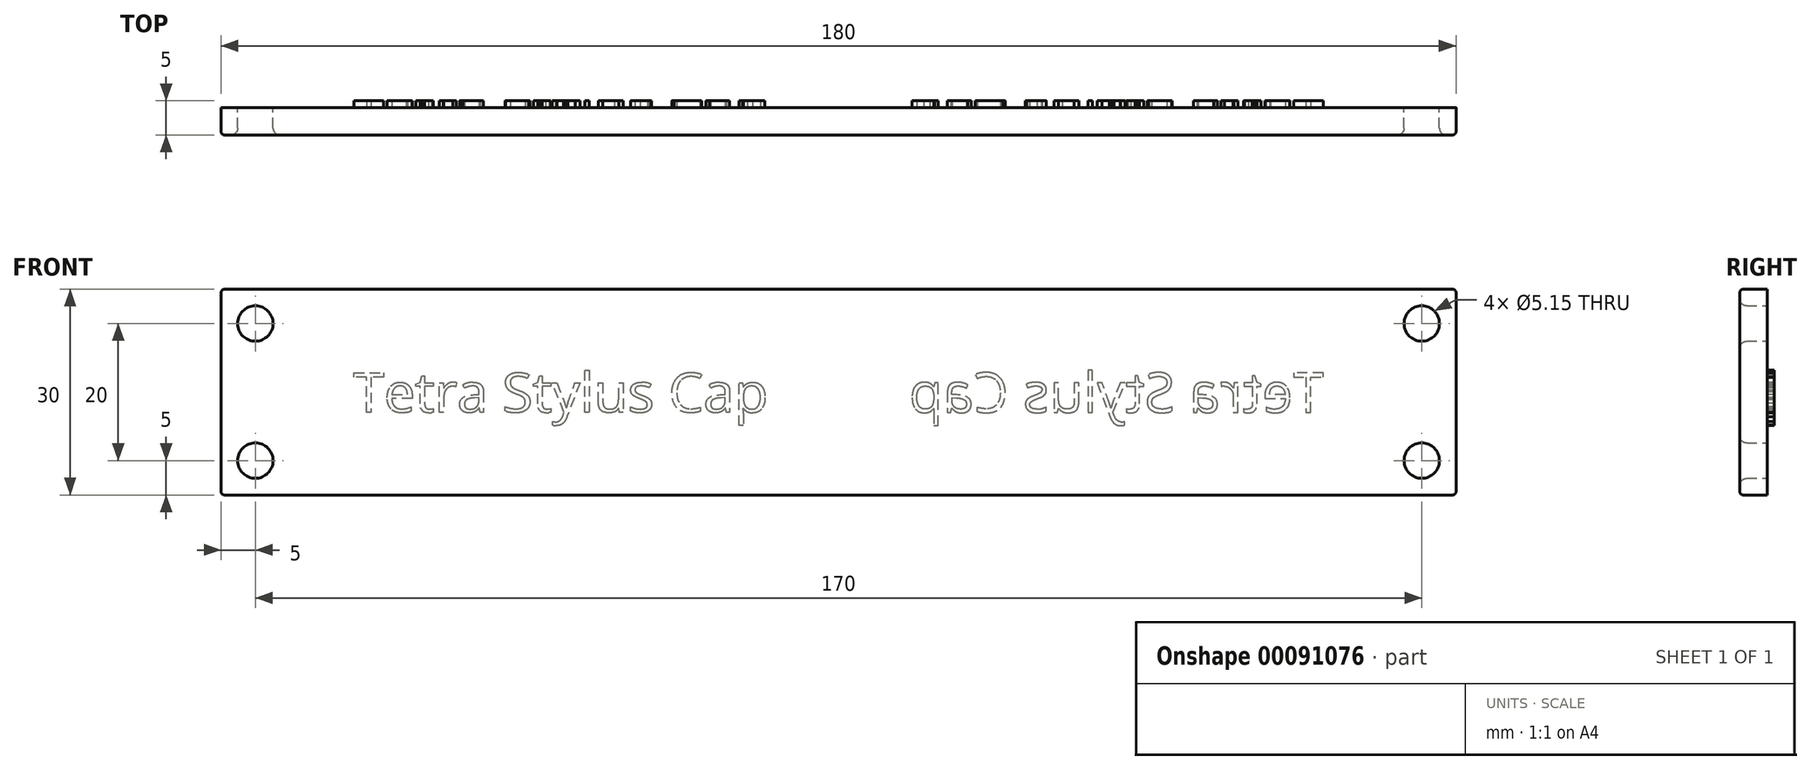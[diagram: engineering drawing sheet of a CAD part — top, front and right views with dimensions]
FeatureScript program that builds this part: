
annotation { "Feature Type Name" : "Feature", "Feature Type Description" : "" }
export const myFeature = defineFeature(function(context is Context, id is Id, definition is map)
    precondition{}
    {
        {
            var Q0;
            Q0=qCreatedBy(makeId("Front.planeOp"),FACE);
            var sketch = newSketch(context, id + "F0", { "sketchPlane" : qUnion([Q0])});
            skLineSegment(sketch, "E0.bottom", {"start": v(-90, -15) * mm, "end": v(90, -15) * mm});
            skLineSegment(sketch, "E0.top", {"start": v(-90, 15) * mm, "end": v(90, 15) * mm});
            skLineSegment(sketch, "E0.left", {"start": v(-90, -15) * mm, "end": v(-90, 15) * mm});
            skLineSegment(sketch, "E0.right", {"start": v(90, -15) * mm, "end": v(90, 15) * mm});
            skPoint(sketch, "E0.middle", {"position": v(0, 0) * mm});
            skCircle(sketch, "E1", {"center": v(-85, 10) * mm, "radius": 2.58 * mm});
            skPoint(sketch, "E2.start.orphan", {"position": v(-90, 0) * mm});
            skPoint(sketch, "E3.orphan", {"position": v(0, 15) * mm});
            skPoint(sketch, "E4.end.orphan", {"position": v(0, -15) * mm});
            skLineSegment(sketch, "E5", {"start": v(-90, 0) * mm, "end": v(0, 0) * mm, "construction": true});
            skLineSegment(sketch, "E6", {"start": v(0, 15) * mm, "end": v(0, -15) * mm, "construction": true});
            skCircle(sketch, "E7.MirrorC", {"center": v(-85, -10) * mm, "radius": 2.58 * mm});
            skCircle(sketch, "E8.MirrorC", {"center": v(85, 10) * mm, "radius": 2.58 * mm});
            skCircle(sketch, "E9.MirrorC", {"center": v(85, -10) * mm, "radius": 2.58 * mm});
            skSolve(sketch);
        }
        {
            var Q0;
            Q0=makeQuery(id+"F0.imprint","IMPRINT",FACE,{"disambiguationData":[TD([[makeQuery(id+"F0.imprint","IMPRINT",EDGE,{"derivedFrom":sQuery(id+"F0.wireOp",EDGE,"E0.bottom")}),1.0]])]});
            extrude(context, id + "F1", {"entities" : qUnion([Q0]), "depth" : 4 * mm});
        }
        {
            var Q0;
            Q0=makeQuery(id+"F1.opExtrude","CAP_EDGE",EDGE,{"disambiguationData":[OSD([sQuery(id+"F0.wireOp",EDGE,"E1")])],"isStart":false});
            var Q1;
            Q1=makeQuery(id+"F1.opExtrude","CAP_EDGE",EDGE,{"disambiguationData":[OSD([sQuery(id+"F0.wireOp",EDGE,"f5b72a5b-8583-449a-bdbf-9ac5a681e1fd0.MirrorC")])],"isStart":false});
            var Q2;
            Q2=makeQuery(id+"F1.opExtrude","CAP_EDGE",EDGE,{"disambiguationData":[OSD([sQuery(id+"F0.wireOp",EDGE,"2623e306-60f4-4522-aa65-1e3e8c2cf5b60.MirrorC")])],"isStart":false});
            var Q3;
            Q3=makeQuery(id+"F1.opExtrude","CAP_EDGE",EDGE,{"disambiguationData":[OSD([sQuery(id+"F0.wireOp",EDGE,"be81a34d-1d50-4ce7-a7a8-4484a1701fac0.MirrorC")])],"isStart":false});
            var Q4;
            Q4=makeQuery(id+"F1.opExtrude","CAP_EDGE",EDGE,{"disambiguationData":[OSD([sQuery(id+"F0.wireOp",EDGE,"E7.MirrorC")])],"isStart":false});
            var Q5;
            Q5=makeQuery(id+"F1.opExtrude","CAP_EDGE",EDGE,{"disambiguationData":[OSD([sQuery(id+"F0.wireOp",EDGE,"E8.MirrorC")])],"isStart":false});
            var Q6;
            Q6=makeQuery(id+"F1.opExtrude","CAP_EDGE",EDGE,{"disambiguationData":[OSD([sQuery(id+"F0.wireOp",EDGE,"E9.MirrorC")])],"isStart":false});
            fillet(context, id + "F2", {"entities" : qUnion([Q0, Q1, Q2, Q3, Q4, Q5, Q6]), "radius" : 1 * mm, "tangentPropagation" : true, "allowEdgeOverflow" : false});
        }
        {
            var Q0;
            Q0=makeQuery(id+"F1.opExtrude","CAP_EDGE",EDGE,{"disambiguationData":[OSD([sQuery(id+"F0.wireOp",EDGE,"E0.top")])],"isStart":false});
            var Q1;
            Q1=makeQuery(id+"F1.opExtrude","CAP_EDGE",EDGE,{"disambiguationData":[OSD([sQuery(id+"F0.wireOp",EDGE,"E0.left")])],"isStart":false});
            var Q2;
            Q2=makeQuery(id+"F1.opExtrude","CAP_EDGE",EDGE,{"disambiguationData":[OSD([sQuery(id+"F0.wireOp",EDGE,"E0.bottom")])],"isStart":false});
            var Q3;
            Q3=makeQuery(id+"F1.opExtrude","CAP_EDGE",EDGE,{"disambiguationData":[OSD([sQuery(id+"F0.wireOp",EDGE,"E0.right")])],"isStart":false});
            var Q4;
            Q4=makeQuery(id+"F1.opExtrude","SWEPT_EDGE",EDGE,{"disambiguationData":[OSD([sQuery(id+"F0.wireOp",EDGE,"E0.top"),sQuery(id+"F0.wireOp",EDGE,"E0.left")])]});
            var Q5;
            Q5=makeQuery(id+"F1.opExtrude","SWEPT_EDGE",EDGE,{"disambiguationData":[OSD([sQuery(id+"F0.wireOp",EDGE,"E0.bottom"),sQuery(id+"F0.wireOp",EDGE,"E0.left")])]});
            var Q6;
            Q6=makeQuery(id+"F1.opExtrude","SWEPT_EDGE",EDGE,{"disambiguationData":[OSD([sQuery(id+"F0.wireOp",EDGE,"E0.top"),sQuery(id+"F0.wireOp",EDGE,"E0.right")])]});
            var Q7;
            Q7=makeQuery(id+"F1.opExtrude","SWEPT_EDGE",EDGE,{"disambiguationData":[OSD([sQuery(id+"F0.wireOp",EDGE,"E0.bottom"),sQuery(id+"F0.wireOp",EDGE,"E0.right")])]});
            fillet(context, id + "F3", {"entities" : qUnion([Q0, Q1, Q2, Q3, Q4, Q5, Q6, Q7]), "radius" : .5 * mm, "tangentPropagation" : true, "allowEdgeOverflow" : false});
        }
        {
            var Q0;
            Q0=makeQuery(id+"F1.opExtrude","CAP_FACE",FACE,{"disambiguationData":[OSD([sQuery(id+"F0.wireOp",EDGE,"E0.bottom"),sQuery(id+"F0.wireOp",EDGE,"E0.top"),sQuery(id+"F0.wireOp",EDGE,"E0.left"),sQuery(id+"F0.wireOp",EDGE,"E0.right"),sQuery(id+"F0.wireOp",EDGE,"E1"),sQuery(id+"F0.wireOp",EDGE,"E7.MirrorC"),sQuery(id+"F0.wireOp",EDGE,"E8.MirrorC"),sQuery(id+"F0.wireOp",EDGE,"E9.MirrorC")])],"isStart":true});
            var sketch = newSketch(context, id + "F4", { "sketchPlane" : qUnion([Q0])});
            skText(sketch, "E10", { "text": "Tetra Stylus Cap", "fontName": "OpenSans-Regular.ttf"});
            skLineSegment(sketch, "E11", {"start": v(0, 15) * mm, "end": v(0, -15) * mm, "construction": true});
            const initialGuessF4  = {"E10": [-0.0707, -0.00295, 1, 0, 0.0058]};
            skSetInitialGuess(sketch, initialGuessF4);
            skSolve(sketch);
        }
        {
            var Q0;
            Q0=qSketchRegion(id+"F4",true);
            extrude(context, id + "F5", {"entities" : qUnion([Q0]), "operationType" : NewBodyOperationType.ADD, "depth" : 1 * mm});
        }
        {
            var Q0;
            Q0=makeQuery(id+"F1.opExtrude","SWEPT_BODY",BODY,{"disambiguationData":[OSD([sQuery(id+"F0.wireOp",EDGE,"E0.bottom"),sQuery(id+"F0.wireOp",EDGE,"E0.top"),sQuery(id+"F0.wireOp",EDGE,"E0.left"),sQuery(id+"F0.wireOp",EDGE,"E0.right"),sQuery(id+"F0.wireOp",EDGE,"E1"),sQuery(id+"F0.wireOp",EDGE,"E7.MirrorC"),sQuery(id+"F0.wireOp",EDGE,"E8.MirrorC"),sQuery(id+"F0.wireOp",EDGE,"E9.MirrorC")])]});
            var Q1;
            Q1=makeQuery(id+"F5.opExtrude","SWEPT_FACE",FACE,{"disambiguationData":[OSD([sQuery(id+"F4.wireOp",EDGE,"E10.sketch_text.stroke-94")])]});
            var Q2;
            Q2=makeQuery(id+"F5.opExtrude","SWEPT_FACE",FACE,{"disambiguationData":[OSD([sQuery(id+"F4.wireOp",EDGE,"E10.sketch_text.stroke-169")])]});
            var Q3;
            Q3=makeQuery(id+"F5.opExtrude","SWEPT_FACE",FACE,{"disambiguationData":[OSD([sQuery(id+"F4.wireOp",EDGE,"E10.sketch_text.stroke-185")])]});
            var Q4;
            Q4=makeQuery(id+"F5.opExtrude","SWEPT_FACE",FACE,{"disambiguationData":[OSD([sQuery(id+"F4.wireOp",EDGE,"E10.sketch_text.stroke-125")])]});
            var Q5;
            Q5=makeQuery(id+"F5.opExtrude","SWEPT_FACE",FACE,{"disambiguationData":[OSD([sQuery(id+"F4.wireOp",EDGE,"E10.sketch_text.stroke-155")])]});
            var Q6;
            Q6=makeQuery(id+"F5.opExtrude","SWEPT_FACE",FACE,{"disambiguationData":[OSD([sQuery(id+"F4.wireOp",EDGE,"E10.sketch_text.stroke-65")])]});
            var Q7;
            Q7=makeQuery(id+"F5.opExtrude","SWEPT_FACE",FACE,{"disambiguationData":[OSD([sQuery(id+"F4.wireOp",EDGE,"E10.sketch_text.stroke-81")])]});
            var Q8;
            Q8=makeQuery(id+"F5.opExtrude","SWEPT_FACE",FACE,{"disambiguationData":[OSD([sQuery(id+"F4.wireOp",EDGE,"E10.sketch_text.stroke-67")])]});
            var Q9;
            Q9=makeQuery(id+"F5.opExtrude","SWEPT_FACE",FACE,{"disambiguationData":[OSD([sQuery(id+"F4.wireOp",EDGE,"E10.sketch_text.stroke-99")])]});
            var Q10;
            Q10=makeQuery(id+"F5.opExtrude","SWEPT_FACE",FACE,{"disambiguationData":[OSD([sQuery(id+"F4.wireOp",EDGE,"E10.sketch_text.stroke-127")])]});
            var Q11;
            Q11=makeQuery(id+"F5.opExtrude","SWEPT_FACE",FACE,{"disambiguationData":[OSD([sQuery(id+"F4.wireOp",EDGE,"E10.sketch_text.stroke-10")])]});
            var Q12;
            Q12=makeQuery(id+"F5.opExtrude","CAP_FACE",FACE,{"disambiguationData":[OSD([sQuery(id+"F4.wireOp",EDGE,"E10.sketch_text.stroke-9"),sQuery(id+"F4.wireOp",EDGE,"E10.sketch_text.stroke-10"),sQuery(id+"F4.wireOp",EDGE,"E10.sketch_text.stroke-11"),sQuery(id+"F4.wireOp",EDGE,"E10.sketch_text.stroke-12")])],"isStart":false});
            var Q13;
            Q13=makeQuery(id+"F5.opExtrude","SWEPT_FACE",FACE,{"disambiguationData":[OSD([sQuery(id+"F4.wireOp",EDGE,"E10.sketch_text.stroke-154")])]});
            var Q14;
            Q14=makeQuery(id+"F5.opExtrude","SWEPT_FACE",FACE,{"disambiguationData":[OSD([sQuery(id+"F4.wireOp",EDGE,"E10.sketch_text.stroke-1")])]});
            var Q15;
            Q15=makeQuery(id+"F5.opExtrude","CAP_FACE",FACE,{"disambiguationData":[OSD([sQuery(id+"F4.wireOp",EDGE,"E10.sketch_text.stroke-124"),sQuery(id+"F4.wireOp",EDGE,"E10.sketch_text.stroke-125"),sQuery(id+"F4.wireOp",EDGE,"E10.sketch_text.stroke-126"),sQuery(id+"F4.wireOp",EDGE,"E10.sketch_text.stroke-127"),sQuery(id+"F4.wireOp",EDGE,"E10.sketch_text.stroke-128"),sQuery(id+"F4.wireOp",EDGE,"E10.sketch_text.stroke-129"),sQuery(id+"F4.wireOp",EDGE,"E10.sketch_text.stroke-130"),sQuery(id+"F4.wireOp",EDGE,"E10.sketch_text.stroke-131"),sQuery(id+"F4.wireOp",EDGE,"E10.sketch_text.stroke-132"),sQuery(id+"F4.wireOp",EDGE,"E10.sketch_text.stroke-133"),sQuery(id+"F4.wireOp",EDGE,"E10.sketch_text.stroke-134"),sQuery(id+"F4.wireOp",EDGE,"E10.sketch_text.stroke-135"),sQuery(id+"F4.wireOp",EDGE,"E10.sketch_text.stroke-136"),sQuery(id+"F4.wireOp",EDGE,"E10.sketch_text.stroke-137"),sQuery(id+"F4.wireOp",EDGE,"E10.sketch_text.stroke-138")])],"isStart":false});
            var Q16;
            Q16=makeQuery(id+"F5.opExtrude","CAP_FACE",FACE,{"disambiguationData":[OSD([sQuery(id+"F4.wireOp",EDGE,"E10.sketch_text.stroke-34"),sQuery(id+"F4.wireOp",EDGE,"E10.sketch_text.stroke-35"),sQuery(id+"F4.wireOp",EDGE,"E10.sketch_text.stroke-36"),sQuery(id+"F4.wireOp",EDGE,"E10.sketch_text.stroke-37"),sQuery(id+"F4.wireOp",EDGE,"E10.sketch_text.stroke-38"),sQuery(id+"F4.wireOp",EDGE,"E10.sketch_text.stroke-39"),sQuery(id+"F4.wireOp",EDGE,"E10.sketch_text.stroke-40"),sQuery(id+"F4.wireOp",EDGE,"E10.sketch_text.stroke-41"),sQuery(id+"F4.wireOp",EDGE,"E10.sketch_text.stroke-42"),sQuery(id+"F4.wireOp",EDGE,"E10.sketch_text.stroke-43"),sQuery(id+"F4.wireOp",EDGE,"E10.sketch_text.stroke-44"),sQuery(id+"F4.wireOp",EDGE,"E10.sketch_text.stroke-45"),sQuery(id+"F4.wireOp",EDGE,"E10.sketch_text.stroke-46"),sQuery(id+"F4.wireOp",EDGE,"E10.sketch_text.stroke-47"),sQuery(id+"F4.wireOp",EDGE,"E10.sketch_text.stroke-48"),sQuery(id+"F4.wireOp",EDGE,"E10.sketch_text.stroke-49"),sQuery(id+"F4.wireOp",EDGE,"E10.sketch_text.stroke-50"),sQuery(id+"F4.wireOp",EDGE,"E10.sketch_text.stroke-51"),sQuery(id+"F4.wireOp",EDGE,"E10.sketch_text.stroke-52"),sQuery(id+"F4.wireOp",EDGE,"E10.sketch_text.stroke-53"),sQuery(id+"F4.wireOp",EDGE,"E10.sketch_text.stroke-54"),sQuery(id+"F4.wireOp",EDGE,"E10.sketch_text.stroke-55"),sQuery(id+"F4.wireOp",EDGE,"E10.sketch_text.stroke-56"),sQuery(id+"F4.wireOp",EDGE,"E10.sketch_text.stroke-57"),sQuery(id+"F4.wireOp",EDGE,"E10.sketch_text.stroke-58"),sQuery(id+"F4.wireOp",EDGE,"E10.sketch_text.stroke-59"),sQuery(id+"F4.wireOp",EDGE,"E10.sketch_text.stroke-60")])],"isStart":false});
            var Q17;
            Q17=makeQuery(id+"F5.opExtrude","SWEPT_FACE",FACE,{"disambiguationData":[OSD([sQuery(id+"F4.wireOp",EDGE,"E10.sketch_text.stroke-50")])]});
            var Q18;
            Q18=makeQuery(id+"F5.opExtrude","SWEPT_FACE",FACE,{"disambiguationData":[OSD([sQuery(id+"F4.wireOp",EDGE,"E10.sketch_text.stroke-2")])]});
            var Q19;
            Q19=makeQuery(id+"F5.opExtrude","SWEPT_FACE",FACE,{"disambiguationData":[OSD([sQuery(id+"F4.wireOp",EDGE,"E10.sketch_text.stroke-3")])]});
            var Q20;
            Q20=makeQuery(id+"F5.opExtrude","SWEPT_FACE",FACE,{"disambiguationData":[OSD([sQuery(id+"F4.wireOp",EDGE,"E10.sketch_text.stroke-5")])]});
            var Q21;
            Q21=makeQuery(id+"F5.opExtrude","SWEPT_FACE",FACE,{"disambiguationData":[OSD([sQuery(id+"F4.wireOp",EDGE,"E10.sketch_text.stroke-8")])]});
            var Q22;
            Q22=makeQuery(id+"F5.opExtrude","SWEPT_FACE",FACE,{"disambiguationData":[OSD([sQuery(id+"F4.wireOp",EDGE,"E10.sketch_text.stroke-98")])]});
            var Q23;
            Q23=makeQuery(id+"F5.opExtrude","SWEPT_FACE",FACE,{"disambiguationData":[OSD([sQuery(id+"F4.wireOp",EDGE,"E10.sketch_text.stroke-66")])]});
            var Q24;
            Q24=makeQuery(id+"F5.opExtrude","SWEPT_FACE",FACE,{"disambiguationData":[OSD([sQuery(id+"F4.wireOp",EDGE,"E10.sketch_text.stroke-153")])]});
            var Q25;
            Q25=makeQuery(id+"F5.opExtrude","SWEPT_FACE",FACE,{"disambiguationData":[OSD([sQuery(id+"F4.wireOp",EDGE,"E10.sketch_text.stroke-126")])]});
            var Q26;
            Q26=makeQuery(id+"F5.opExtrude","SWEPT_FACE",FACE,{"disambiguationData":[OSD([sQuery(id+"F4.wireOp",EDGE,"E10.sketch_text.stroke-183")])]});
            var Q27;
            Q27=makeQuery(id+"F5.opExtrude","SWEPT_FACE",FACE,{"disambiguationData":[OSD([sQuery(id+"F4.wireOp",EDGE,"E10.sketch_text.stroke-109")])]});
            var Q28;
            Q28=makeQuery(id+"F5.opExtrude","SWEPT_FACE",FACE,{"disambiguationData":[OSD([sQuery(id+"F4.wireOp",EDGE,"E10.sketch_text.stroke-186")])]});
            var Q29;
            Q29=makeQuery(id+"F5.opExtrude","SWEPT_FACE",FACE,{"disambiguationData":[OSD([sQuery(id+"F4.wireOp",EDGE,"E10.sketch_text.stroke-79")])]});
            var Q30;
            Q30=makeQuery(id+"F5.opExtrude","SWEPT_FACE",FACE,{"disambiguationData":[OSD([sQuery(id+"F4.wireOp",EDGE,"E10.sketch_text.stroke-110")])]});
            var Q31;
            Q31=makeQuery(id+"F5.opExtrude","SWEPT_FACE",FACE,{"disambiguationData":[OSD([sQuery(id+"F4.wireOp",EDGE,"E10.sketch_text.stroke-38")])]});
            var Q32;
            Q32=makeQuery(id+"F5.opExtrude","SWEPT_FACE",FACE,{"disambiguationData":[OSD([sQuery(id+"F4.wireOp",EDGE,"E10.sketch_text.stroke-24")])]});
            var Q33;
            Q33=makeQuery(id+"F5.opExtrude","SWEPT_FACE",FACE,{"disambiguationData":[OSD([sQuery(id+"F4.wireOp",EDGE,"E10.sketch_text.stroke-12")])]});
            var Q34;
            Q34=makeQuery(id+"F5.opExtrude","SWEPT_FACE",FACE,{"disambiguationData":[OSD([sQuery(id+"F4.wireOp",EDGE,"E10.sketch_text.stroke-100")])]});
            var Q35;
            Q35=makeQuery(id+"F5.opExtrude","SWEPT_FACE",FACE,{"disambiguationData":[OSD([sQuery(id+"F4.wireOp",EDGE,"E10.sketch_text.stroke-158")])]});
            var Q36;
            Q36=makeQuery(id+"F5.opExtrude","SWEPT_FACE",FACE,{"disambiguationData":[OSD([sQuery(id+"F4.wireOp",EDGE,"E10.sketch_text.stroke-142")])]});
            var Q37;
            Q37=makeQuery(id+"F5.opExtrude","SWEPT_FACE",FACE,{"disambiguationData":[OSD([sQuery(id+"F4.wireOp",EDGE,"E10.sketch_text.stroke-54")])]});
            var Q38;
            Q38=makeQuery(id+"F5.opExtrude","SWEPT_FACE",FACE,{"disambiguationData":[OSD([sQuery(id+"F4.wireOp",EDGE,"E10.sketch_text.stroke-25")])]});
            var Q39;
            Q39=makeQuery(id+"F5.opExtrude","SWEPT_FACE",FACE,{"disambiguationData":[OSD([sQuery(id+"F4.wireOp",EDGE,"E10.sketch_text.stroke-101")])]});
            var Q40;
            Q40=makeQuery(id+"F5.opExtrude","SWEPT_FACE",FACE,{"disambiguationData":[OSD([sQuery(id+"F4.wireOp",EDGE,"E10.sketch_text.stroke-69")])]});
            var Q41;
            Q41=makeQuery(id+"F5.opExtrude","SWEPT_FACE",FACE,{"disambiguationData":[OSD([sQuery(id+"F4.wireOp",EDGE,"E10.sketch_text.stroke-159")])]});
            var Q42;
            Q42=makeQuery(id+"F5.opExtrude","SWEPT_FACE",FACE,{"disambiguationData":[OSD([sQuery(id+"F4.wireOp",EDGE,"E10.sketch_text.stroke-85")])]});
            var Q43;
            Q43=makeQuery(id+"F5.opExtrude","SWEPT_FACE",FACE,{"disambiguationData":[OSD([sQuery(id+"F4.wireOp",EDGE,"E10.sketch_text.stroke-173")])]});
            var Q44;
            Q44=makeQuery(id+"F5.opExtrude","SWEPT_FACE",FACE,{"disambiguationData":[OSD([sQuery(id+"F4.wireOp",EDGE,"E10.sketch_text.stroke-40")])]});
            var Q45;
            Q45=makeQuery(id+"F5.opExtrude","SWEPT_FACE",FACE,{"disambiguationData":[OSD([sQuery(id+"F4.wireOp",EDGE,"E10.sketch_text.stroke-102")])]});
            var Q46;
            Q46=makeQuery(id+"F5.opExtrude","SWEPT_FACE",FACE,{"disambiguationData":[OSD([sQuery(id+"F4.wireOp",EDGE,"E10.sketch_text.stroke-86")])]});
            var Q47;
            Q47=makeQuery(id+"F5.opExtrude","SWEPT_FACE",FACE,{"disambiguationData":[OSD([sQuery(id+"F4.wireOp",EDGE,"E10.sketch_text.stroke-130")])]});
            var Q48;
            Q48=makeQuery(id+"F5.opExtrude","SWEPT_FACE",FACE,{"disambiguationData":[OSD([sQuery(id+"F4.wireOp",EDGE,"E10.sketch_text.stroke-103")])]});
            var Q49;
            Q49=makeQuery(id+"F5.opExtrude","SWEPT_FACE",FACE,{"disambiguationData":[OSD([sQuery(id+"F4.wireOp",EDGE,"E10.sketch_text.stroke-87")])]});
            var Q50;
            Q50=makeQuery(id+"F5.opExtrude","SWEPT_FACE",FACE,{"disambiguationData":[OSD([sQuery(id+"F4.wireOp",EDGE,"E10.sketch_text.stroke-145")])]});
            var Q51;
            Q51=makeQuery(id+"F5.opExtrude","SWEPT_FACE",FACE,{"disambiguationData":[OSD([sQuery(id+"F4.wireOp",EDGE,"E10.sketch_text.stroke-131")])]});
            var Q52;
            Q52=makeQuery(id+"F5.opExtrude","SWEPT_FACE",FACE,{"disambiguationData":[OSD([sQuery(id+"F4.wireOp",EDGE,"E10.sketch_text.stroke-28")])]});
            var Q53;
            Q53=makeQuery(id+"F5.opExtrude","SWEPT_FACE",FACE,{"disambiguationData":[OSD([sQuery(id+"F4.wireOp",EDGE,"E10.sketch_text.stroke-14")])]});
            var Q54;
            Q54=makeQuery(id+"F5.opExtrude","SWEPT_FACE",FACE,{"disambiguationData":[OSD([sQuery(id+"F4.wireOp",EDGE,"E10.sketch_text.stroke-88")])]});
            var Q55;
            Q55=makeQuery(id+"F5.opExtrude","SWEPT_FACE",FACE,{"disambiguationData":[OSD([sQuery(id+"F4.wireOp",EDGE,"E10.sketch_text.stroke-162")])]});
            var Q56;
            Q56=makeQuery(id+"F5.opExtrude","SWEPT_FACE",FACE,{"disambiguationData":[OSD([sQuery(id+"F4.wireOp",EDGE,"E10.sketch_text.stroke-176")])]});
            var Q57;
            Q57=makeQuery(id+"F5.opExtrude","SWEPT_FACE",FACE,{"disambiguationData":[OSD([sQuery(id+"F4.wireOp",EDGE,"E10.sketch_text.stroke-73")])]});
            var Q58;
            Q58=makeQuery(id+"F5.opExtrude","SWEPT_FACE",FACE,{"disambiguationData":[OSD([sQuery(id+"F4.wireOp",EDGE,"E10.sketch_text.stroke-59")])]});
            var Q59;
            Q59=makeQuery(id+"F5.opExtrude","SWEPT_FACE",FACE,{"disambiguationData":[OSD([sQuery(id+"F4.wireOp",EDGE,"E10.sketch_text.stroke-133")])]});
            var Q60;
            Q60=makeQuery(id+"F5.opExtrude","SWEPT_FACE",FACE,{"disambiguationData":[OSD([sQuery(id+"F4.wireOp",EDGE,"E10.sketch_text.stroke-119")])]});
            var Q61;
            Q61=makeQuery(id+"F5.opExtrude","SWEPT_FACE",FACE,{"disambiguationData":[OSD([sQuery(id+"F4.wireOp",EDGE,"E10.sketch_text.stroke-74")])]});
            var Q62;
            Q62=makeQuery(id+"F5.opExtrude","SWEPT_FACE",FACE,{"disambiguationData":[OSD([sQuery(id+"F4.wireOp",EDGE,"E10.sketch_text.stroke-44")])]});
            var Q63;
            Q63=makeQuery(id+"F5.opExtrude","SWEPT_FACE",FACE,{"disambiguationData":[OSD([sQuery(id+"F4.wireOp",EDGE,"E10.sketch_text.stroke-120")])]});
            var Q64;
            Q64=makeQuery(id+"F5.opExtrude","SWEPT_FACE",FACE,{"disambiguationData":[OSD([sQuery(id+"F4.wireOp",EDGE,"E10.sketch_text.stroke-90")])]});
            var Q65;
            Q65=makeQuery(id+"F5.opExtrude","SWEPT_FACE",FACE,{"disambiguationData":[OSD([sQuery(id+"F4.wireOp",EDGE,"E10.sketch_text.stroke-178")])]});
            var Q66;
            Q66=makeQuery(id+"F5.opExtrude","SWEPT_FACE",FACE,{"disambiguationData":[OSD([sQuery(id+"F4.wireOp",EDGE,"E10.sketch_text.stroke-45")])]});
            var Q67;
            Q67=makeQuery(id+"F5.opExtrude","SWEPT_FACE",FACE,{"disambiguationData":[OSD([sQuery(id+"F4.wireOp",EDGE,"E10.sketch_text.stroke-31")])]});
            var Q68;
            Q68=makeQuery(id+"F5.opExtrude","SWEPT_FACE",FACE,{"disambiguationData":[OSD([sQuery(id+"F4.wireOp",EDGE,"E10.sketch_text.stroke-135")])]});
            var Q69;
            Q69=makeQuery(id+"F5.opExtrude","SWEPT_FACE",FACE,{"disambiguationData":[OSD([sQuery(id+"F4.wireOp",EDGE,"E10.sketch_text.stroke-179")])]});
            var Q70;
            Q70=makeQuery(id+"F5.opExtrude","SWEPT_FACE",FACE,{"disambiguationData":[OSD([sQuery(id+"F4.wireOp",EDGE,"E10.sketch_text.stroke-165")])]});
            var Q71;
            Q71=makeQuery(id+"F5.opExtrude","SWEPT_FACE",FACE,{"disambiguationData":[OSD([sQuery(id+"F4.wireOp",EDGE,"E10.sketch_text.stroke-149")])]});
            var Q72;
            Q72=makeQuery(id+"F5.opExtrude","SWEPT_FACE",FACE,{"disambiguationData":[OSD([sQuery(id+"F4.wireOp",EDGE,"E10.sketch_text.stroke-136")])]});
            var Q73;
            Q73=makeQuery(id+"F5.opExtrude","SWEPT_FACE",FACE,{"disambiguationData":[OSD([sQuery(id+"F4.wireOp",EDGE,"E10.sketch_text.stroke-122")])]});
            var Q74;
            Q74=makeQuery(id+"F5.opExtrude","SWEPT_FACE",FACE,{"disambiguationData":[OSD([sQuery(id+"F4.wireOp",EDGE,"E10.sketch_text.stroke-106")])]});
            var Q75;
            Q75=makeQuery(id+"F5.opExtrude","SWEPT_FACE",FACE,{"disambiguationData":[OSD([sQuery(id+"F4.wireOp",EDGE,"E10.sketch_text.stroke-180")])]});
            var Q76;
            Q76=makeQuery(id+"F5.opExtrude","SWEPT_FACE",FACE,{"disambiguationData":[OSD([sQuery(id+"F4.wireOp",EDGE,"E10.sketch_text.stroke-166")])]});
            var Q77;
            Q77=makeQuery(id+"F5.opExtrude","SWEPT_FACE",FACE,{"disambiguationData":[OSD([sQuery(id+"F4.wireOp",EDGE,"E10.sketch_text.stroke-150")])]});
            var Q78;
            Q78=makeQuery(id+"F5.opExtrude","SWEPT_FACE",FACE,{"disambiguationData":[OSD([sQuery(id+"F4.wireOp",EDGE,"E10.sketch_text.stroke-76")])]});
            var Q79;
            Q79=makeQuery(id+"F5.opExtrude","SWEPT_FACE",FACE,{"disambiguationData":[OSD([sQuery(id+"F4.wireOp",EDGE,"E10.sketch_text.stroke-32")])]});
            var Q80;
            Q80=makeQuery(id+"F5.opExtrude","SWEPT_FACE",FACE,{"disambiguationData":[OSD([sQuery(id+"F4.wireOp",EDGE,"E10.sketch_text.stroke-181")])]});
            var Q81;
            Q81=makeQuery(id+"F5.opExtrude","SWEPT_FACE",FACE,{"disambiguationData":[OSD([sQuery(id+"F4.wireOp",EDGE,"E10.sketch_text.stroke-47")])]});
            var Q82;
            Q82=makeQuery(id+"F5.opExtrude","SWEPT_FACE",FACE,{"disambiguationData":[OSD([sQuery(id+"F4.wireOp",EDGE,"E10.sketch_text.stroke-123")])]});
            var Q83;
            Q83=makeQuery(id+"F5.opExtrude","SWEPT_FACE",FACE,{"disambiguationData":[OSD([sQuery(id+"F4.wireOp",EDGE,"E10.sketch_text.stroke-107")])]});
            var Q84;
            Q84=makeQuery(id+"F5.opExtrude","SWEPT_FACE",FACE,{"disambiguationData":[OSD([sQuery(id+"F4.wireOp",EDGE,"E10.sketch_text.stroke-48")])]});
            var Q85;
            Q85=makeQuery(id+"F5.opExtrude","SWEPT_FACE",FACE,{"disambiguationData":[OSD([sQuery(id+"F4.wireOp",EDGE,"E10.sketch_text.stroke-124")])]});
            var Q86;
            Q86=makeQuery(id+"F5.opExtrude","SWEPT_FACE",FACE,{"disambiguationData":[OSD([sQuery(id+"F4.wireOp",EDGE,"E10.sketch_text.stroke-108")])]});
            var Q87;
            Q87=makeQuery(id+"F5.opExtrude","CAP_FACE",FACE,{"disambiguationData":[OSD([sQuery(id+"F4.wireOp",EDGE,"E10.sketch_text.stroke-139"),sQuery(id+"F4.wireOp",EDGE,"E10.sketch_text.stroke-140"),sQuery(id+"F4.wireOp",EDGE,"E10.sketch_text.stroke-141"),sQuery(id+"F4.wireOp",EDGE,"E10.sketch_text.stroke-142"),sQuery(id+"F4.wireOp",EDGE,"E10.sketch_text.stroke-143"),sQuery(id+"F4.wireOp",EDGE,"E10.sketch_text.stroke-144"),sQuery(id+"F4.wireOp",EDGE,"E10.sketch_text.stroke-145"),sQuery(id+"F4.wireOp",EDGE,"E10.sketch_text.stroke-146"),sQuery(id+"F4.wireOp",EDGE,"E10.sketch_text.stroke-147"),sQuery(id+"F4.wireOp",EDGE,"E10.sketch_text.stroke-148"),sQuery(id+"F4.wireOp",EDGE,"E10.sketch_text.stroke-149"),sQuery(id+"F4.wireOp",EDGE,"E10.sketch_text.stroke-150"),sQuery(id+"F4.wireOp",EDGE,"E10.sketch_text.stroke-151"),sQuery(id+"F4.wireOp",EDGE,"E10.sketch_text.stroke-152"),sQuery(id+"F4.wireOp",EDGE,"E10.sketch_text.stroke-153"),sQuery(id+"F4.wireOp",EDGE,"E10.sketch_text.stroke-154"),sQuery(id+"F4.wireOp",EDGE,"E10.sketch_text.stroke-155"),sQuery(id+"F4.wireOp",EDGE,"E10.sketch_text.stroke-156"),sQuery(id+"F4.wireOp",EDGE,"E10.sketch_text.stroke-157"),sQuery(id+"F4.wireOp",EDGE,"E10.sketch_text.stroke-158"),sQuery(id+"F4.wireOp",EDGE,"E10.sketch_text.stroke-159"),sQuery(id+"F4.wireOp",EDGE,"E10.sketch_text.stroke-160"),sQuery(id+"F4.wireOp",EDGE,"E10.sketch_text.stroke-161"),sQuery(id+"F4.wireOp",EDGE,"E10.sketch_text.stroke-162"),sQuery(id+"F4.wireOp",EDGE,"E10.sketch_text.stroke-163"),sQuery(id+"F4.wireOp",EDGE,"E10.sketch_text.stroke-164"),sQuery(id+"F4.wireOp",EDGE,"E10.sketch_text.stroke-165")])],"isStart":false});
            var Q88;
            Q88=makeQuery(id+"F5.opExtrude","CAP_FACE",FACE,{"disambiguationData":[OSD([sQuery(id+"F4.wireOp",EDGE,"E10.sketch_text.stroke-21"),sQuery(id+"F4.wireOp",EDGE,"E10.sketch_text.stroke-22"),sQuery(id+"F4.wireOp",EDGE,"E10.sketch_text.stroke-23"),sQuery(id+"F4.wireOp",EDGE,"E10.sketch_text.stroke-24"),sQuery(id+"F4.wireOp",EDGE,"E10.sketch_text.stroke-25"),sQuery(id+"F4.wireOp",EDGE,"E10.sketch_text.stroke-26"),sQuery(id+"F4.wireOp",EDGE,"E10.sketch_text.stroke-27"),sQuery(id+"F4.wireOp",EDGE,"E10.sketch_text.stroke-28"),sQuery(id+"F4.wireOp",EDGE,"E10.sketch_text.stroke-29"),sQuery(id+"F4.wireOp",EDGE,"E10.sketch_text.stroke-30"),sQuery(id+"F4.wireOp",EDGE,"E10.sketch_text.stroke-31"),sQuery(id+"F4.wireOp",EDGE,"E10.sketch_text.stroke-32"),sQuery(id+"F4.wireOp",EDGE,"E10.sketch_text.stroke-33")])],"isStart":false});
            var Q89;
            Q89=makeQuery(id+"F5.opExtrude","SWEPT_FACE",FACE,{"disambiguationData":[OSD([sQuery(id+"F4.wireOp",EDGE,"E10.sketch_text.stroke-113")])]});
            var Q90;
            Q90=makeQuery(id+"F5.opExtrude","SWEPT_FACE",FACE,{"disambiguationData":[OSD([sQuery(id+"F4.wireOp",EDGE,"E10.sketch_text.stroke-37")])]});
            var Q91;
            Q91=makeQuery(id+"F5.opExtrude","SWEPT_FACE",FACE,{"disambiguationData":[OSD([sQuery(id+"F4.wireOp",EDGE,"E10.sketch_text.stroke-187")])]});
            var Q92;
            Q92=makeQuery(id+"F5.opExtrude","SWEPT_FACE",FACE,{"disambiguationData":[OSD([sQuery(id+"F4.wireOp",EDGE,"E10.sketch_text.stroke-0")])]});
            var Q93;
            Q93=makeQuery(id+"F5.opExtrude","SWEPT_FACE",FACE,{"disambiguationData":[OSD([sQuery(id+"F4.wireOp",EDGE,"E10.sketch_text.stroke-4")])]});
            var Q94;
            Q94=makeQuery(id+"F5.opExtrude","SWEPT_FACE",FACE,{"disambiguationData":[OSD([sQuery(id+"F4.wireOp",EDGE,"E10.sketch_text.stroke-82")])]});
            var Q95;
            Q95=makeQuery(id+"F5.opExtrude","SWEPT_FACE",FACE,{"disambiguationData":[OSD([sQuery(id+"F4.wireOp",EDGE,"E10.sketch_text.stroke-52")])]});
            var Q96;
            Q96=makeQuery(id+"F5.opExtrude","SWEPT_FACE",FACE,{"disambiguationData":[OSD([sQuery(id+"F4.wireOp",EDGE,"E10.sketch_text.stroke-49")])]});
            var Q97;
            Q97=makeQuery(id+"F5.opExtrude","SWEPT_FACE",FACE,{"disambiguationData":[OSD([sQuery(id+"F4.wireOp",EDGE,"E10.sketch_text.stroke-63")])]});
            var Q98;
            Q98=makeQuery(id+"F5.opExtrude","SWEPT_FACE",FACE,{"disambiguationData":[OSD([sQuery(id+"F4.wireOp",EDGE,"E10.sketch_text.stroke-21")])]});
            var Q99;
            Q99=makeQuery(id+"F5.opExtrude","SWEPT_FACE",FACE,{"disambiguationData":[OSD([sQuery(id+"F4.wireOp",EDGE,"E10.sketch_text.stroke-128")])]});
            var Q100;
            Q100=makeQuery(id+"F5.opExtrude","SWEPT_FACE",FACE,{"disambiguationData":[OSD([sQuery(id+"F4.wireOp",EDGE,"E10.sketch_text.stroke-55")])]});
            var Q101;
            Q101=makeQuery(id+"F5.opExtrude","SWEPT_FACE",FACE,{"disambiguationData":[OSD([sQuery(id+"F4.wireOp",EDGE,"E10.sketch_text.stroke-26")])]});
            var Q102;
            Q102=makeQuery(id+"F5.opExtrude","SWEPT_FACE",FACE,{"disambiguationData":[OSD([sQuery(id+"F4.wireOp",EDGE,"E10.sketch_text.stroke-174")])]});
            var Q103;
            Q103=makeQuery(id+"F5.opExtrude","SWEPT_FACE",FACE,{"disambiguationData":[OSD([sQuery(id+"F4.wireOp",EDGE,"E10.sketch_text.stroke-104")])]});
            var Q104;
            Q104=makeQuery(id+"F5.opExtrude","SWEPT_FACE",FACE,{"disambiguationData":[OSD([sQuery(id+"F4.wireOp",EDGE,"E10.sketch_text.stroke-72")])]});
            var Q105;
            Q105=makeQuery(id+"F5.opExtrude","SWEPT_FACE",FACE,{"disambiguationData":[OSD([sQuery(id+"F4.wireOp",EDGE,"E10.sketch_text.stroke-132")])]});
            var Q106;
            Q106=makeQuery(id+"F5.opExtrude","SWEPT_FACE",FACE,{"disambiguationData":[OSD([sQuery(id+"F4.wireOp",EDGE,"E10.sketch_text.stroke-43")])]});
            var Q107;
            Q107=makeQuery(id+"F5.opExtrude","SWEPT_FACE",FACE,{"disambiguationData":[OSD([sQuery(id+"F4.wireOp",EDGE,"E10.sketch_text.stroke-15")])]});
            var Q108;
            Q108=makeQuery(id+"F5.opExtrude","SWEPT_FACE",FACE,{"disambiguationData":[OSD([sQuery(id+"F4.wireOp",EDGE,"E10.sketch_text.stroke-89")])]});
            var Q109;
            Q109=makeQuery(id+"F5.opExtrude","SWEPT_FACE",FACE,{"disambiguationData":[OSD([sQuery(id+"F4.wireOp",EDGE,"E10.sketch_text.stroke-163")])]});
            var Q110;
            Q110=makeQuery(id+"F5.opExtrude","SWEPT_FACE",FACE,{"disambiguationData":[OSD([sQuery(id+"F4.wireOp",EDGE,"E10.sketch_text.stroke-30")])]});
            var Q111;
            Q111=makeQuery(id+"F5.opExtrude","SWEPT_FACE",FACE,{"disambiguationData":[OSD([sQuery(id+"F4.wireOp",EDGE,"E10.sketch_text.stroke-134")])]});
            var Q112;
            Q112=makeQuery(id+"F5.opExtrude","SWEPT_FACE",FACE,{"disambiguationData":[OSD([sQuery(id+"F4.wireOp",EDGE,"E10.sketch_text.stroke-121")])]});
            var Q113;
            Q113=makeQuery(id+"F5.opExtrude","CAP_FACE",FACE,{"disambiguationData":[OSD([sQuery(id+"F4.wireOp",EDGE,"E10.sketch_text.stroke-105"),sQuery(id+"F4.wireOp",EDGE,"E10.sketch_text.stroke-106"),sQuery(id+"F4.wireOp",EDGE,"E10.sketch_text.stroke-107"),sQuery(id+"F4.wireOp",EDGE,"E10.sketch_text.stroke-108"),sQuery(id+"F4.wireOp",EDGE,"E10.sketch_text.stroke-109"),sQuery(id+"F4.wireOp",EDGE,"E10.sketch_text.stroke-110"),sQuery(id+"F4.wireOp",EDGE,"E10.sketch_text.stroke-111"),sQuery(id+"F4.wireOp",EDGE,"E10.sketch_text.stroke-112"),sQuery(id+"F4.wireOp",EDGE,"E10.sketch_text.stroke-113"),sQuery(id+"F4.wireOp",EDGE,"E10.sketch_text.stroke-114"),sQuery(id+"F4.wireOp",EDGE,"E10.sketch_text.stroke-115"),sQuery(id+"F4.wireOp",EDGE,"E10.sketch_text.stroke-116"),sQuery(id+"F4.wireOp",EDGE,"E10.sketch_text.stroke-117"),sQuery(id+"F4.wireOp",EDGE,"E10.sketch_text.stroke-118"),sQuery(id+"F4.wireOp",EDGE,"E10.sketch_text.stroke-119"),sQuery(id+"F4.wireOp",EDGE,"E10.sketch_text.stroke-120"),sQuery(id+"F4.wireOp",EDGE,"E10.sketch_text.stroke-121"),sQuery(id+"F4.wireOp",EDGE,"E10.sketch_text.stroke-122"),sQuery(id+"F4.wireOp",EDGE,"E10.sketch_text.stroke-123")])],"isStart":false});
            var Q114;
            Q114=makeQuery(id+"F5.opExtrude","SWEPT_FACE",FACE,{"disambiguationData":[OSD([sQuery(id+"F4.wireOp",EDGE,"E10.sketch_text.stroke-92")])]});
            var Q115;
            Q115=makeQuery(id+"F5.opExtrude","SWEPT_FACE",FACE,{"disambiguationData":[OSD([sQuery(id+"F4.wireOp",EDGE,"E10.sketch_text.stroke-46")])]});
            var Q116;
            Q116=makeQuery(id+"F5.opExtrude","CAP_FACE",FACE,{"disambiguationData":[OSD([sQuery(id+"F4.wireOp",EDGE,"E10.sketch_text.stroke-61"),sQuery(id+"F4.wireOp",EDGE,"E10.sketch_text.stroke-62"),sQuery(id+"F4.wireOp",EDGE,"E10.sketch_text.stroke-63"),sQuery(id+"F4.wireOp",EDGE,"E10.sketch_text.stroke-64"),sQuery(id+"F4.wireOp",EDGE,"E10.sketch_text.stroke-65"),sQuery(id+"F4.wireOp",EDGE,"E10.sketch_text.stroke-66"),sQuery(id+"F4.wireOp",EDGE,"E10.sketch_text.stroke-67"),sQuery(id+"F4.wireOp",EDGE,"E10.sketch_text.stroke-68"),sQuery(id+"F4.wireOp",EDGE,"E10.sketch_text.stroke-69"),sQuery(id+"F4.wireOp",EDGE,"E10.sketch_text.stroke-70"),sQuery(id+"F4.wireOp",EDGE,"E10.sketch_text.stroke-71"),sQuery(id+"F4.wireOp",EDGE,"E10.sketch_text.stroke-72"),sQuery(id+"F4.wireOp",EDGE,"E10.sketch_text.stroke-73"),sQuery(id+"F4.wireOp",EDGE,"E10.sketch_text.stroke-74"),sQuery(id+"F4.wireOp",EDGE,"E10.sketch_text.stroke-75"),sQuery(id+"F4.wireOp",EDGE,"E10.sketch_text.stroke-76"),sQuery(id+"F4.wireOp",EDGE,"E10.sketch_text.stroke-77"),sQuery(id+"F4.wireOp",EDGE,"E10.sketch_text.stroke-78"),sQuery(id+"F4.wireOp",EDGE,"E10.sketch_text.stroke-79"),sQuery(id+"F4.wireOp",EDGE,"E10.sketch_text.stroke-80"),sQuery(id+"F4.wireOp",EDGE,"E10.sketch_text.stroke-81"),sQuery(id+"F4.wireOp",EDGE,"E10.sketch_text.stroke-82"),sQuery(id+"F4.wireOp",EDGE,"E10.sketch_text.stroke-83"),sQuery(id+"F4.wireOp",EDGE,"E10.sketch_text.stroke-84"),sQuery(id+"F4.wireOp",EDGE,"E10.sketch_text.stroke-85"),sQuery(id+"F4.wireOp",EDGE,"E10.sketch_text.stroke-86"),sQuery(id+"F4.wireOp",EDGE,"E10.sketch_text.stroke-87"),sQuery(id+"F4.wireOp",EDGE,"E10.sketch_text.stroke-88"),sQuery(id+"F4.wireOp",EDGE,"E10.sketch_text.stroke-89"),sQuery(id+"F4.wireOp",EDGE,"E10.sketch_text.stroke-90"),sQuery(id+"F4.wireOp",EDGE,"E10.sketch_text.stroke-91"),sQuery(id+"F4.wireOp",EDGE,"E10.sketch_text.stroke-92"),sQuery(id+"F4.wireOp",EDGE,"E10.sketch_text.stroke-93"),sQuery(id+"F4.wireOp",EDGE,"E10.sketch_text.stroke-94"),sQuery(id+"F4.wireOp",EDGE,"E10.sketch_text.stroke-95"),sQuery(id+"F4.wireOp",EDGE,"E10.sketch_text.stroke-96"),sQuery(id+"F4.wireOp",EDGE,"E10.sketch_text.stroke-97"),sQuery(id+"F4.wireOp",EDGE,"E10.sketch_text.stroke-98"),sQuery(id+"F4.wireOp",EDGE,"E10.sketch_text.stroke-99"),sQuery(id+"F4.wireOp",EDGE,"E10.sketch_text.stroke-100"),sQuery(id+"F4.wireOp",EDGE,"E10.sketch_text.stroke-101"),sQuery(id+"F4.wireOp",EDGE,"E10.sketch_text.stroke-102"),sQuery(id+"F4.wireOp",EDGE,"E10.sketch_text.stroke-103"),sQuery(id+"F4.wireOp",EDGE,"E10.sketch_text.stroke-104")])],"isStart":false});
            var Q117;
            Q117=makeQuery(id+"F5.opExtrude","SWEPT_FACE",FACE,{"disambiguationData":[OSD([sQuery(id+"F4.wireOp",EDGE,"E10.sketch_text.stroke-33")])]});
            var Q118;
            Q118=makeQuery(id+"F5.opExtrude","SWEPT_FACE",FACE,{"disambiguationData":[OSD([sQuery(id+"F4.wireOp",EDGE,"E10.sketch_text.stroke-93")])]});
            var Q119;
            Q119=makeQuery(id+"F5.opExtrude","SWEPT_FACE",FACE,{"disambiguationData":[OSD([sQuery(id+"F4.wireOp",EDGE,"E10.sketch_text.stroke-34")])]});
            var Q120;
            Q120=makeQuery(id+"F5.opExtrude","SWEPT_FACE",FACE,{"disambiguationData":[OSD([sQuery(id+"F4.wireOp",EDGE,"E10.sketch_text.stroke-152")])]});
            var Q121;
            Q121=makeQuery(id+"F5.opExtrude","SWEPT_FACE",FACE,{"disambiguationData":[OSD([sQuery(id+"F4.wireOp",EDGE,"E10.sketch_text.stroke-51")])]});
            var Q122;
            Q122=makeQuery(id+"F5.opExtrude","SWEPT_FACE",FACE,{"disambiguationData":[OSD([sQuery(id+"F4.wireOp",EDGE,"E10.sketch_text.stroke-6")])]});
            var Q123;
            Q123=makeQuery(id+"F5.opExtrude","SWEPT_FACE",FACE,{"disambiguationData":[OSD([sQuery(id+"F4.wireOp",EDGE,"E10.sketch_text.stroke-7")])]});
            var Q124;
            Q124=makeQuery(id+"F5.opExtrude","SWEPT_FACE",FACE,{"disambiguationData":[OSD([sQuery(id+"F4.wireOp",EDGE,"E10.sketch_text.stroke-156")])]});
            var Q125;
            Q125=makeQuery(id+"F5.opExtrude","SWEPT_FACE",FACE,{"disambiguationData":[OSD([sQuery(id+"F4.wireOp",EDGE,"E10.sketch_text.stroke-112")])]});
            var Q126;
            Q126=makeQuery(id+"F5.boolean.opBoolean","SPLIT",FACE,{"disambiguationData":[TD([makeQuery(id+"F5.opExtrude","SWEPT_FACE",FACE,{"disambiguationData":[OSD([sQuery(id+"F4.wireOp",EDGE,"E10.sketch_text.stroke-182")])]})])],"derivedFrom":makeQuery(id+"F1.opExtrude","CAP_FACE",FACE,{"disambiguationData":[OSD([sQuery(id+"F0.wireOp",EDGE,"E0.bottom"),sQuery(id+"F0.wireOp",EDGE,"E0.top"),sQuery(id+"F0.wireOp",EDGE,"E0.left"),sQuery(id+"F0.wireOp",EDGE,"E0.right"),sQuery(id+"F0.wireOp",EDGE,"E1"),sQuery(id+"F0.wireOp",EDGE,"E7.MirrorC"),sQuery(id+"F0.wireOp",EDGE,"E8.MirrorC"),sQuery(id+"F0.wireOp",EDGE,"E9.MirrorC")])],"isStart":true})});
            var Q127;
            Q127=makeQuery(id+"F5.opExtrude","SWEPT_FACE",FACE,{"disambiguationData":[OSD([sQuery(id+"F4.wireOp",EDGE,"E10.sketch_text.stroke-96")])]});
            var Q128;
            Q128=makeQuery(id+"F5.opExtrude","SWEPT_FACE",FACE,{"disambiguationData":[OSD([sQuery(id+"F4.wireOp",EDGE,"E10.sketch_text.stroke-114")])]});
            var Q129;
            Q129=makeQuery(id+"F5.opExtrude","SWEPT_FACE",FACE,{"disambiguationData":[OSD([sQuery(id+"F4.wireOp",EDGE,"E10.sketch_text.stroke-39")])]});
            var Q130;
            Q130=makeQuery(id+"F5.opExtrude","SWEPT_FACE",FACE,{"disambiguationData":[OSD([sQuery(id+"F4.wireOp",EDGE,"E10.sketch_text.stroke-13")])]});
            var Q131;
            Q131=makeQuery(id+"F5.opExtrude","SWEPT_FACE",FACE,{"disambiguationData":[OSD([sQuery(id+"F4.wireOp",EDGE,"E10.sketch_text.stroke-115")])]});
            var Q132;
            Q132=makeQuery(id+"F5.opExtrude","SWEPT_FACE",FACE,{"disambiguationData":[OSD([sQuery(id+"F4.wireOp",EDGE,"E10.sketch_text.stroke-56")])]});
            var Q133;
            Q133=makeQuery(id+"F5.opExtrude","SWEPT_FACE",FACE,{"disambiguationData":[OSD([sQuery(id+"F4.wireOp",EDGE,"E10.sketch_text.stroke-144")])]});
            var Q134;
            Q134=makeQuery(id+"F5.opExtrude","SWEPT_FACE",FACE,{"disambiguationData":[OSD([sQuery(id+"F4.wireOp",EDGE,"E10.sketch_text.stroke-190")])]});
            var Q135;
            Q135=makeQuery(id+"F5.opExtrude","SWEPT_FACE",FACE,{"disambiguationData":[OSD([sQuery(id+"F4.wireOp",EDGE,"E10.sketch_text.stroke-116")])]});
            var Q136;
            Q136=makeQuery(id+"F5.opExtrude","SWEPT_FACE",FACE,{"disambiguationData":[OSD([sQuery(id+"F4.wireOp",EDGE,"E10.sketch_text.stroke-41")])]});
            var Q137;
            Q137=makeQuery(id+"F5.opExtrude","SWEPT_FACE",FACE,{"disambiguationData":[OSD([sQuery(id+"F4.wireOp",EDGE,"E10.sketch_text.stroke-161")])]});
            var Q138;
            Q138=makeQuery(id+"F5.opExtrude","SWEPT_FACE",FACE,{"disambiguationData":[OSD([sQuery(id+"F4.wireOp",EDGE,"E10.sketch_text.stroke-146")])]});
            var Q139;
            Q139=makeQuery(id+"F5.opExtrude","SWEPT_FACE",FACE,{"disambiguationData":[OSD([sQuery(id+"F4.wireOp",EDGE,"E10.sketch_text.stroke-58")])]});
            var Q140;
            Q140=makeQuery(id+"F5.opExtrude","SWEPT_FACE",FACE,{"disambiguationData":[OSD([sQuery(id+"F4.wireOp",EDGE,"E10.sketch_text.stroke-105")])]});
            var Q141;
            Q141=makeQuery(id+"F5.opExtrude","SWEPT_FACE",FACE,{"disambiguationData":[OSD([sQuery(id+"F4.wireOp",EDGE,"E10.sketch_text.stroke-177")])]});
            var Q142;
            Q142=makeQuery(id+"F5.opExtrude","SWEPT_FACE",FACE,{"disambiguationData":[OSD([sQuery(id+"F4.wireOp",EDGE,"E10.sketch_text.stroke-77")])]});
            var Q143;
            Q143=makeQuery(id+"F5.opExtrude","SWEPT_FACE",FACE,{"disambiguationData":[OSD([sQuery(id+"F4.wireOp",EDGE,"E10.sketch_text.stroke-138")])]});
            var Q144;
            Q144=makeQuery(id+"F5.opExtrude","SWEPT_FACE",FACE,{"disambiguationData":[OSD([sQuery(id+"F4.wireOp",EDGE,"E10.sketch_text.stroke-111")])]});
            var Q145;
            Q145=makeQuery(id+"F5.opExtrude","SWEPT_FACE",FACE,{"disambiguationData":[OSD([sQuery(id+"F4.wireOp",EDGE,"E10.sketch_text.stroke-53")])]});
            var Q146;
            Q146=makeQuery(id+"F5.opExtrude","SWEPT_FACE",FACE,{"disambiguationData":[OSD([sQuery(id+"F4.wireOp",EDGE,"E10.sketch_text.stroke-141")])]});
            var Q147;
            Q147=makeQuery(id+"F5.opExtrude","SWEPT_FACE",FACE,{"disambiguationData":[OSD([sQuery(id+"F4.wireOp",EDGE,"E10.sketch_text.stroke-157")])]});
            var Q148;
            Q148=makeQuery(id+"F5.opExtrude","SWEPT_FACE",FACE,{"disambiguationData":[OSD([sQuery(id+"F4.wireOp",EDGE,"E10.sketch_text.stroke-64")])]});
            var Q149;
            Q149=makeQuery(id+"F5.boolean.opBoolean","SPLIT",FACE,{"disambiguationData":[TD([makeQuery(id+"F5.opExtrude","SWEPT_FACE",FACE,{"disambiguationData":[OSD([sQuery(id+"F4.wireOp",EDGE,"E10.sketch_text.stroke-53")])]})])],"derivedFrom":makeQuery(id+"F1.opExtrude","CAP_FACE",FACE,{"disambiguationData":[OSD([sQuery(id+"F0.wireOp",EDGE,"E0.bottom"),sQuery(id+"F0.wireOp",EDGE,"E0.top"),sQuery(id+"F0.wireOp",EDGE,"E0.left"),sQuery(id+"F0.wireOp",EDGE,"E0.right"),sQuery(id+"F0.wireOp",EDGE,"E1"),sQuery(id+"F0.wireOp",EDGE,"E7.MirrorC"),sQuery(id+"F0.wireOp",EDGE,"E8.MirrorC"),sQuery(id+"F0.wireOp",EDGE,"E9.MirrorC")])],"isStart":true})});
            var Q150;
            Q150=makeQuery(id+"F5.opExtrude","SWEPT_FACE",FACE,{"disambiguationData":[OSD([sQuery(id+"F4.wireOp",EDGE,"E10.sketch_text.stroke-36")])]});
            var Q151;
            Q151=makeQuery(id+"F5.opExtrude","SWEPT_FACE",FACE,{"disambiguationData":[OSD([sQuery(id+"F4.wireOp",EDGE,"E10.sketch_text.stroke-22")])]});
            var Q152;
            Q152=makeQuery(id+"F5.boolean.opBoolean","SPLIT",FACE,{"disambiguationData":[TD([makeQuery(id+"F5.opExtrude","SWEPT_FACE",FACE,{"disambiguationData":[OSD([sQuery(id+"F4.wireOp",EDGE,"E10.sketch_text.stroke-119")])]})])],"derivedFrom":makeQuery(id+"F1.opExtrude","CAP_FACE",FACE,{"disambiguationData":[OSD([sQuery(id+"F0.wireOp",EDGE,"E0.bottom"),sQuery(id+"F0.wireOp",EDGE,"E0.top"),sQuery(id+"F0.wireOp",EDGE,"E0.left"),sQuery(id+"F0.wireOp",EDGE,"E0.right"),sQuery(id+"F0.wireOp",EDGE,"E1"),sQuery(id+"F0.wireOp",EDGE,"E7.MirrorC"),sQuery(id+"F0.wireOp",EDGE,"E8.MirrorC"),sQuery(id+"F0.wireOp",EDGE,"E9.MirrorC")])],"isStart":true})});
            var Q153;
            Q153=makeQuery(id+"F5.boolean.opBoolean","SPLIT",FACE,{"disambiguationData":[TD([makeQuery(id+"F5.opExtrude","SWEPT_FACE",FACE,{"disambiguationData":[OSD([sQuery(id+"F4.wireOp",EDGE,"E10.sketch_text.stroke-158")])]})])],"derivedFrom":makeQuery(id+"F1.opExtrude","CAP_FACE",FACE,{"disambiguationData":[OSD([sQuery(id+"F0.wireOp",EDGE,"E0.bottom"),sQuery(id+"F0.wireOp",EDGE,"E0.top"),sQuery(id+"F0.wireOp",EDGE,"E0.left"),sQuery(id+"F0.wireOp",EDGE,"E0.right"),sQuery(id+"F0.wireOp",EDGE,"E1"),sQuery(id+"F0.wireOp",EDGE,"E7.MirrorC"),sQuery(id+"F0.wireOp",EDGE,"E8.MirrorC"),sQuery(id+"F0.wireOp",EDGE,"E9.MirrorC")])],"isStart":true})});
            var Q154;
            Q154=makeQuery(id+"F5.opExtrude","SWEPT_FACE",FACE,{"disambiguationData":[OSD([sQuery(id+"F4.wireOp",EDGE,"E10.sketch_text.stroke-9")])]});
            var Q155;
            Q155=makeQuery(id+"F5.opExtrude","SWEPT_FACE",FACE,{"disambiguationData":[OSD([sQuery(id+"F4.wireOp",EDGE,"E10.sketch_text.stroke-167")])]});
            var Q156;
            Q156=makeQuery(id+"F5.opExtrude","SWEPT_FACE",FACE,{"disambiguationData":[OSD([sQuery(id+"F4.wireOp",EDGE,"E10.sketch_text.stroke-95")])]});
            var Q157;
            Q157=makeQuery(id+"F5.opExtrude","SWEPT_FACE",FACE,{"disambiguationData":[OSD([sQuery(id+"F4.wireOp",EDGE,"E10.sketch_text.stroke-184")])]});
            var Q158;
            Q158=makeQuery(id+"F5.opExtrude","SWEPT_FACE",FACE,{"disambiguationData":[OSD([sQuery(id+"F4.wireOp",EDGE,"E10.sketch_text.stroke-84")])]});
            var Q159;
            Q159=makeQuery(id+"F5.opExtrude","SWEPT_FACE",FACE,{"disambiguationData":[OSD([sQuery(id+"F4.wireOp",EDGE,"E10.sketch_text.stroke-68")])]});
            var Q160;
            Q160=makeQuery(id+"F5.opExtrude","SWEPT_FACE",FACE,{"disambiguationData":[OSD([sQuery(id+"F4.wireOp",EDGE,"E10.sketch_text.stroke-143")])]});
            var Q161;
            Q161=makeQuery(id+"F5.opExtrude","SWEPT_FACE",FACE,{"disambiguationData":[OSD([sQuery(id+"F4.wireOp",EDGE,"E10.sketch_text.stroke-189")])]});
            var Q162;
            Q162=makeQuery(id+"F5.opExtrude","CAP_FACE",FACE,{"disambiguationData":[OSD([sQuery(id+"F4.wireOp",EDGE,"E10.sketch_text.stroke-13"),sQuery(id+"F4.wireOp",EDGE,"E10.sketch_text.stroke-14"),sQuery(id+"F4.wireOp",EDGE,"E10.sketch_text.stroke-15"),sQuery(id+"F4.wireOp",EDGE,"E10.sketch_text.stroke-16"),sQuery(id+"F4.wireOp",EDGE,"E10.sketch_text.stroke-17"),sQuery(id+"F4.wireOp",EDGE,"E10.sketch_text.stroke-18"),sQuery(id+"F4.wireOp",EDGE,"E10.sketch_text.stroke-19"),sQuery(id+"F4.wireOp",EDGE,"E10.sketch_text.stroke-20")])],"isStart":false});
            var Q163;
            Q163=makeQuery(id+"F5.opExtrude","SWEPT_FACE",FACE,{"disambiguationData":[OSD([sQuery(id+"F4.wireOp",EDGE,"E10.sketch_text.stroke-57")])]});
            var Q164;
            Q164=makeQuery(id+"F5.opExtrude","SWEPT_FACE",FACE,{"disambiguationData":[OSD([sQuery(id+"F4.wireOp",EDGE,"E10.sketch_text.stroke-29")])]});
            var Q165;
            Q165=makeQuery(id+"F5.opExtrude","SWEPT_FACE",FACE,{"disambiguationData":[OSD([sQuery(id+"F4.wireOp",EDGE,"E10.sketch_text.stroke-60")])]});
            var Q166;
            Q166=makeQuery(id+"F5.opExtrude","SWEPT_FACE",FACE,{"disambiguationData":[OSD([sQuery(id+"F4.wireOp",EDGE,"E10.sketch_text.stroke-148")])]});
            var Q167;
            Q167=makeQuery(id+"F5.opExtrude","SWEPT_FACE",FACE,{"disambiguationData":[OSD([sQuery(id+"F4.wireOp",EDGE,"E10.sketch_text.stroke-75")])]});
            var Q168;
            Q168=makeQuery(id+"F5.opExtrude","SWEPT_FACE",FACE,{"disambiguationData":[OSD([sQuery(id+"F4.wireOp",EDGE,"E10.sketch_text.stroke-91")])]});
            var Q169;
            Q169=makeQuery(id+"F5.opExtrude","SWEPT_FACE",FACE,{"disambiguationData":[OSD([sQuery(id+"F4.wireOp",EDGE,"E10.sketch_text.stroke-78")])]});
            var Q170;
            Q170=makeQuery(id+"F5.opExtrude","SWEPT_FACE",FACE,{"disambiguationData":[OSD([sQuery(id+"F4.wireOp",EDGE,"E10.sketch_text.stroke-62")])]});
            var Q171;
            Q171=makeQuery(id+"F5.opExtrude","SWEPT_FACE",FACE,{"disambiguationData":[OSD([sQuery(id+"F4.wireOp",EDGE,"E10.sketch_text.stroke-182")])]});
            var Q172;
            Q172=makeQuery(id+"F5.opExtrude","SWEPT_FACE",FACE,{"disambiguationData":[OSD([sQuery(id+"F4.wireOp",EDGE,"E10.sketch_text.stroke-11")])]});
            var Q173;
            Q173=makeQuery(id+"F5.opExtrude","SWEPT_FACE",FACE,{"disambiguationData":[OSD([sQuery(id+"F4.wireOp",EDGE,"E10.sketch_text.stroke-97")])]});
            var Q174;
            Q174=makeQuery(id+"F5.opExtrude","SWEPT_FACE",FACE,{"disambiguationData":[OSD([sQuery(id+"F4.wireOp",EDGE,"E10.sketch_text.stroke-23")])]});
            var Q175;
            Q175=makeQuery(id+"F5.opExtrude","SWEPT_FACE",FACE,{"disambiguationData":[OSD([sQuery(id+"F4.wireOp",EDGE,"E10.sketch_text.stroke-80")])]});
            var Q176;
            Q176=makeQuery(id+"F5.boolean.opBoolean","SPLIT",FACE,{"disambiguationData":[TD([makeQuery(id+"F5.opExtrude","SWEPT_FACE",FACE,{"disambiguationData":[OSD([sQuery(id+"F4.wireOp",EDGE,"E10.sketch_text.stroke-99")])]})])],"derivedFrom":makeQuery(id+"F1.opExtrude","CAP_FACE",FACE,{"disambiguationData":[OSD([sQuery(id+"F0.wireOp",EDGE,"E0.bottom"),sQuery(id+"F0.wireOp",EDGE,"E0.top"),sQuery(id+"F0.wireOp",EDGE,"E0.left"),sQuery(id+"F0.wireOp",EDGE,"E0.right"),sQuery(id+"F0.wireOp",EDGE,"E1"),sQuery(id+"F0.wireOp",EDGE,"E7.MirrorC"),sQuery(id+"F0.wireOp",EDGE,"E8.MirrorC"),sQuery(id+"F0.wireOp",EDGE,"E9.MirrorC")])],"isStart":true})});
            var Q177;
            Q177=makeQuery(id+"F5.opExtrude","SWEPT_FACE",FACE,{"disambiguationData":[OSD([sQuery(id+"F4.wireOp",EDGE,"E10.sketch_text.stroke-168")])]});
            var Q178;
            Q178=makeQuery(id+"F5.opExtrude","SWEPT_FACE",FACE,{"disambiguationData":[OSD([sQuery(id+"F4.wireOp",EDGE,"E10.sketch_text.stroke-188")])]});
            var Q179;
            Q179=makeQuery(id+"F5.opExtrude","SWEPT_FACE",FACE,{"disambiguationData":[OSD([sQuery(id+"F4.wireOp",EDGE,"E10.sketch_text.stroke-129")])]});
            var Q180;
            Q180=makeQuery(id+"F5.opExtrude","SWEPT_FACE",FACE,{"disambiguationData":[OSD([sQuery(id+"F4.wireOp",EDGE,"E10.sketch_text.stroke-27")])]});
            var Q181;
            Q181=makeQuery(id+"F5.opExtrude","SWEPT_FACE",FACE,{"disambiguationData":[OSD([sQuery(id+"F4.wireOp",EDGE,"E10.sketch_text.stroke-175")])]});
            var Q182;
            Q182=makeQuery(id+"F5.opExtrude","SWEPT_FACE",FACE,{"disambiguationData":[OSD([sQuery(id+"F4.wireOp",EDGE,"E10.sketch_text.stroke-42")])]});
            var Q183;
            Q183=makeQuery(id+"F5.opExtrude","SWEPT_FACE",FACE,{"disambiguationData":[OSD([sQuery(id+"F4.wireOp",EDGE,"E10.sketch_text.stroke-118")])]});
            var Q184;
            Q184=makeQuery(id+"F5.opExtrude","SWEPT_FACE",FACE,{"disambiguationData":[OSD([sQuery(id+"F4.wireOp",EDGE,"E10.sketch_text.stroke-151")])]});
            var Q185;
            Q185=makeQuery(id+"F5.opExtrude","SWEPT_FACE",FACE,{"disambiguationData":[OSD([sQuery(id+"F4.wireOp",EDGE,"E10.sketch_text.stroke-137")])]});
            var Q186;
            Q186=makeQuery(id+"F5.opExtrude","SWEPT_FACE",FACE,{"disambiguationData":[OSD([sQuery(id+"F4.wireOp",EDGE,"E10.sketch_text.stroke-83")])]});
            var Q187;
            Q187=makeQuery(id+"F5.boolean.opBoolean","SPLIT",FACE,{"disambiguationData":[TD([makeQuery(id+"F5.opExtrude","SWEPT_FACE",FACE,{"disambiguationData":[OSD([sQuery(id+"F4.wireOp",EDGE,"E10.sketch_text.stroke-90")])]})])],"derivedFrom":makeQuery(id+"F1.opExtrude","CAP_FACE",FACE,{"disambiguationData":[OSD([sQuery(id+"F0.wireOp",EDGE,"E0.bottom"),sQuery(id+"F0.wireOp",EDGE,"E0.top"),sQuery(id+"F0.wireOp",EDGE,"E0.left"),sQuery(id+"F0.wireOp",EDGE,"E0.right"),sQuery(id+"F0.wireOp",EDGE,"E1"),sQuery(id+"F0.wireOp",EDGE,"E7.MirrorC"),sQuery(id+"F0.wireOp",EDGE,"E8.MirrorC"),sQuery(id+"F0.wireOp",EDGE,"E9.MirrorC")])],"isStart":true})});
            var Q188;
            Q188=makeQuery(id+"F5.opExtrude","SWEPT_FACE",FACE,{"disambiguationData":[OSD([sQuery(id+"F4.wireOp",EDGE,"E10.sketch_text.stroke-139")])]});
            var Q189;
            Q189=makeQuery(id+"F5.opExtrude","SWEPT_FACE",FACE,{"disambiguationData":[OSD([sQuery(id+"F4.wireOp",EDGE,"E10.sketch_text.stroke-70")])]});
            var Q190;
            Q190=makeQuery(id+"F5.opExtrude","SWEPT_FACE",FACE,{"disambiguationData":[OSD([sQuery(id+"F4.wireOp",EDGE,"E10.sketch_text.stroke-160")])]});
            var Q191;
            Q191=makeQuery(id+"F5.opExtrude","SWEPT_FACE",FACE,{"disambiguationData":[OSD([sQuery(id+"F4.wireOp",EDGE,"E10.sketch_text.stroke-71")])]});
            var Q192;
            Q192=makeQuery(id+"F5.opExtrude","SWEPT_FACE",FACE,{"disambiguationData":[OSD([sQuery(id+"F4.wireOp",EDGE,"E10.sketch_text.stroke-117")])]});
            var Q193;
            Q193=makeQuery(id+"F5.opExtrude","SWEPT_FACE",FACE,{"disambiguationData":[OSD([sQuery(id+"F4.wireOp",EDGE,"E10.sketch_text.stroke-147")])]});
            var Q194;
            Q194=makeQuery(id+"F5.opExtrude","SWEPT_FACE",FACE,{"disambiguationData":[OSD([sQuery(id+"F4.wireOp",EDGE,"E10.sketch_text.stroke-164")])]});
            var Q195;
            Q195=makeQuery(id+"F5.opExtrude","SWEPT_FACE",FACE,{"disambiguationData":[OSD([sQuery(id+"F4.wireOp",EDGE,"E10.sketch_text.stroke-61")])]});
            var Q196;
            Q196=makeQuery(id+"F5.opExtrude","SWEPT_FACE",FACE,{"disambiguationData":[OSD([sQuery(id+"F4.wireOp",EDGE,"E10.sketch_text.stroke-19")])]});
            var Q197;
            Q197=makeQuery(id+"F5.opExtrude","SWEPT_FACE",FACE,{"disambiguationData":[OSD([sQuery(id+"F4.wireOp",EDGE,"E10.sketch_text.stroke-35")])]});
            var Q198;
            Q198=makeQuery(id+"F5.opExtrude","SWEPT_FACE",FACE,{"disambiguationData":[OSD([sQuery(id+"F4.wireOp",EDGE,"E10.sketch_text.stroke-140")])]});
            var Q199;
            Q199=makeQuery(id+"F5.opExtrude","SWEPT_FACE",FACE,{"disambiguationData":[OSD([sQuery(id+"F4.wireOp",EDGE,"E10.sketch_text.stroke-20")])]});
            var Q200;
            Q200=makeQuery(id+"F5.opExtrude","SWEPT_FACE",FACE,{"disambiguationData":[OSD([sQuery(id+"F4.wireOp",EDGE,"E10.sketch_text.stroke-16")])]});
            var Q201;
            Q201=makeQuery(id+"F5.opExtrude","SWEPT_FACE",FACE,{"disambiguationData":[OSD([sQuery(id+"F4.wireOp",EDGE,"E10.sketch_text.stroke-18")])]});
            var Q202;
            Q202=makeQuery(id+"F5.opExtrude","SWEPT_FACE",FACE,{"disambiguationData":[OSD([sQuery(id+"F4.wireOp",EDGE,"E10.sketch_text.stroke-17")])]});
            var Q203;
            Q203=qCreatedBy(makeId("Right.planeOp"),FACE);
            mirror(context, id + "F6", {"operationType" : NewBodyOperationType.ADD, "entities" : qUnion([Q0]), "faces" : qUnion([Q1, Q2, Q3, Q4, Q5, Q6, Q7, Q8, Q9, Q10, Q11, Q12, Q13, Q14, Q15, Q16, Q17, Q18, Q19, Q20, Q21, Q22, Q23, Q24, Q25, Q26, Q27, Q28, Q29, Q30, Q31, Q32, Q33, Q34, Q35, Q36, Q37, Q38, Q39, Q40, Q41, Q42, Q43, Q44, Q45, Q46, Q47, Q48, Q49, Q50, Q51, Q52, Q53, Q54, Q55, Q56, Q57, Q58, Q59, Q60, Q61, Q62, Q63, Q64, Q65, Q66, Q67, Q68, Q69, Q70, Q71, Q72, Q73, Q74, Q75, Q76, Q77, Q78, Q79, Q80, Q81, Q82, Q83, Q84, Q85, Q86, Q87, Q88, Q89, Q90, Q91, Q92, Q93, Q94, Q95, Q96, Q97, Q98, Q99, Q100, Q101, Q102, Q103, Q104, Q105, Q106, Q107, Q108, Q109, Q110, Q111, Q112, Q113, Q114, Q115, Q116, Q117, Q118, Q119, Q120, Q121, Q122, Q123, Q124, Q125, Q126, Q127, Q128, Q129, Q130, Q131, Q132, Q133, Q134, Q135, Q136, Q137, Q138, Q139, Q140, Q141, Q142, Q143, Q144, Q145, Q146, Q147, Q148, Q149, Q150, Q151, Q152, Q153, Q154, Q155, Q156, Q157, Q158, Q159, Q160, Q161, Q162, Q163, Q164, Q165, Q166, Q167, Q168, Q169, Q170, Q171, Q172, Q173, Q174, Q175, Q176, Q177, Q178, Q179, Q180, Q181, Q182, Q183, Q184, Q185, Q186, Q187, Q188, Q189, Q190, Q191, Q192, Q193, Q194, Q195, Q196, Q197, Q198, Q199, Q200, Q201, Q202]), "mirrorPlane" : qUnion([Q203])});
        }
    });
